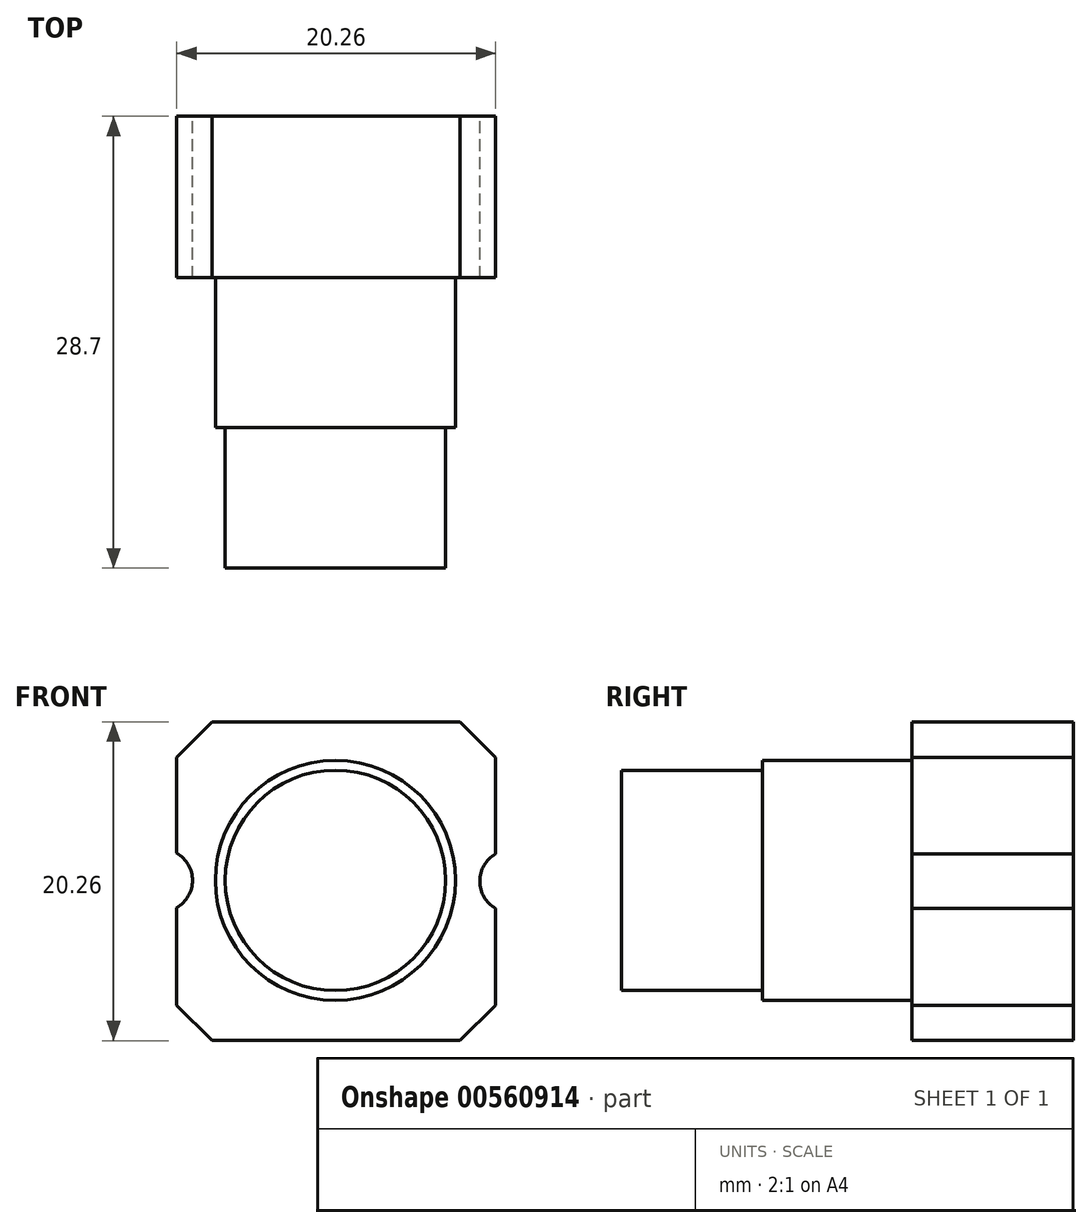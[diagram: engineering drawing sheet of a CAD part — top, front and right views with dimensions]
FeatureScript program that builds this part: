
annotation { "Feature Type Name" : "Feature", "Feature Type Description" : "" }
export const myFeature = defineFeature(function(context is Context, id is Id, definition is map)
    precondition{}
    {
        {
            var Q0;
            Q0=qCreatedBy(makeId("Front.planeOp"),FACE);
            var sketch = newSketch(context, id + "F0", { "sketchPlane" : qUnion([Q0])});
            skCircle(sketch, "E0", {"center": v(0, 0) * mm, "radius": 7.62 * mm});
            skLineSegment(sketch, "E1.bottom", {"start": v(-10.08, 10.07) * mm, "end": v(10.18, 10.07) * mm});
            skLineSegment(sketch, "E1.top", {"start": v(-10.08, -10.18) * mm, "end": v(10.18, -10.18) * mm});
            skLineSegment(sketch, "E1.left", {"start": v(-10.08, 10.07) * mm, "end": v(-10.08, -10.18) * mm});
            skLineSegment(sketch, "E1.right", {"start": v(10.18, 10.07) * mm, "end": v(10.18, -10.18) * mm});
            skCircle(sketch, "E2", {"center": v(11.18, -0.05) * mm, "radius": 2 * mm});
            skPoint(sketch, "E2.centerSnap0", {"position": v(10.18, -0.05) * mm});
            skCircle(sketch, "E3", {"center": v(-11.07, 0) * mm, "radius": 2 * mm});
            skCircle(sketch, "E4", {"center": v(0, 0) * mm, "radius": 7 * mm});
            skSolve(sketch);
        }
        {
            var Q0;
            Q0=makeQuery(id+"F0.imprint","IMPRINT",FACE,{"disambiguationData":[TD([[makeQuery(id+"F0.imprint","IMPRINT",EDGE,{"derivedFrom":sQuery(id+"F0.wireOp",EDGE,"E0")}),-1.0]])]});
            var Q1;
            {var subQ0=sQuery(id+"F0.wireOp",EDGE,"E3");var subQ1=sQuery(id+"F0.wireOp",EDGE,"E1.left");var subQ2=makeQuery(id+"F0.imprint","INTERSECT",VERTEX,{"disambiguationData":[OD(0.0)],"derivedFrom":[subQ1,subQ0]});Q1=makeQuery(id+"F0.imprint","IMPRINT",FACE,{"disambiguationData":[TD([[makeQuery(id+"F0.imprint","IMPRINT",EDGE,{"disambiguationData":[TD([[subQ2,-1.0]])],"derivedFrom":subQ1}),-1.0]])]});}
            var Q2;
            {var subQ0=sQuery(id+"F0.wireOp",EDGE,"E2");var subQ1=sQuery(id+"F0.wireOp",EDGE,"E1.right");var subQ2=makeQuery(id+"F0.imprint","INTERSECT",VERTEX,{"disambiguationData":[OD(0.0)],"derivedFrom":[subQ1,subQ0]});Q2=makeQuery(id+"F0.imprint","IMPRINT",FACE,{"disambiguationData":[TD([[makeQuery(id+"F0.imprint","IMPRINT",EDGE,{"disambiguationData":[TD([[subQ2,-1.0]])],"derivedFrom":subQ1}),1.0]])]});}
            var Q3;
            {var subQ0=sQuery(id+"F0.wireOp",EDGE,"E2");var subQ1=sQuery(id+"F0.wireOp",EDGE,"E1.right");var subQ2=makeQuery(id+"F0.imprint","INTERSECT",VERTEX,{"disambiguationData":[OD(0.0)],"derivedFrom":[subQ1,subQ0]});Q3=makeQuery(id+"F0.imprint","IMPRINT",FACE,{"disambiguationData":[TD([[makeQuery(id+"F0.imprint","IMPRINT",EDGE,{"disambiguationData":[TD([[subQ2,-1.0]])],"derivedFrom":subQ1}),-1.0]])]});}
            var Q4;
            Q4=makeQuery(id+"F0.imprint","IMPRINT",FACE,{"disambiguationData":[TD([[makeQuery(id+"F0.imprint","IMPRINT",EDGE,{"derivedFrom":sQuery(id+"F0.wireOp",EDGE,"E0")}),1.0]])]});
            var Q5;
            Q5=makeQuery(id+"F0.imprint","IMPRINT",FACE,{"disambiguationData":[TD([[makeQuery(id+"F0.imprint","IMPRINT",EDGE,{"derivedFrom":sQuery(id+"F0.wireOp",EDGE,"E4")}),1.0]])]});
            var Q6;
            {var subQ0=sQuery(id+"F0.wireOp",EDGE,"E3");var subQ1=sQuery(id+"F0.wireOp",EDGE,"E1.left");var subQ2=makeQuery(id+"F0.imprint","INTERSECT",VERTEX,{"disambiguationData":[OD(0.0)],"derivedFrom":[subQ1,subQ0]});Q6=makeQuery(id+"F0.imprint","IMPRINT",FACE,{"disambiguationData":[TD([[makeQuery(id+"F0.imprint","IMPRINT",EDGE,{"disambiguationData":[TD([[subQ2,-1.0]])],"derivedFrom":subQ1}),1.0]])]});}
            extrude(context, id + "F1", {"entities" : qUnion([Q0, Q1, Q2, Q3, Q4, Q5, Q6]), "depth" : 10.25 * mm, "offsetDistance" : 25 * mm});
        }
        {
            var Q0;
            Q0=makeQuery(id+"F0.imprint","IMPRINT",FACE,{"disambiguationData":[TD([[makeQuery(id+"F0.imprint","IMPRINT",EDGE,{"derivedFrom":sQuery(id+"F0.wireOp",EDGE,"E0")}),1.0]])]});
            var Q1;
            Q1=makeQuery(id+"F0.imprint","IMPRINT",FACE,{"disambiguationData":[TD([[makeQuery(id+"F0.imprint","IMPRINT",EDGE,{"derivedFrom":sQuery(id+"F0.wireOp",EDGE,"E4")}),1.0]])]});
            extrude(context, id + "F2", {"entities" : qUnion([Q0, Q1]), "operationType" : NewBodyOperationType.ADD, "depth" : 19.75 * mm, "offsetDistance" : 25 * mm});
        }
        {
            var Q0;
            Q0=makeQuery(id+"F0.imprint","IMPRINT",FACE,{"disambiguationData":[TD([[makeQuery(id+"F0.imprint","IMPRINT",EDGE,{"derivedFrom":sQuery(id+"F0.wireOp",EDGE,"E4")}),1.0]])]});
            extrude(context, id + "F3", {"entities" : qUnion([Q0]), "operationType" : NewBodyOperationType.ADD, "depth" : 28.7 * mm, "offsetDistance" : 25 * mm});
        }
        {
            var Q0;
            Q0=makeQuery(id+"F1.opExtrude","SWEPT_EDGE",EDGE,{"disambiguationData":[OSD([sQuery(id+"F0.wireOp",EDGE,"E1.bottom"),sQuery(id+"F0.wireOp",EDGE,"E1.left")])]});
            var Q1;
            Q1=makeQuery(id+"F1.opExtrude","SWEPT_EDGE",EDGE,{"disambiguationData":[OSD([sQuery(id+"F0.wireOp",EDGE,"E1.bottom"),sQuery(id+"F0.wireOp",EDGE,"E1.right")])]});
            var Q2;
            Q2=makeQuery(id+"F1.opExtrude","SWEPT_EDGE",EDGE,{"disambiguationData":[OSD([sQuery(id+"F0.wireOp",EDGE,"E1.top"),sQuery(id+"F0.wireOp",EDGE,"E1.right")])]});
            var Q3;
            Q3=makeQuery(id+"F1.opExtrude","SWEPT_EDGE",EDGE,{"disambiguationData":[OSD([sQuery(id+"F0.wireOp",EDGE,"E1.top"),sQuery(id+"F0.wireOp",EDGE,"E1.left")])]});
            chamfer(context, id + "F4", {"entities" : qUnion([Q0, Q1, Q2, Q3]), "width" : 2.25 * mm, "tangentPropagation" : true});
        }
    });
